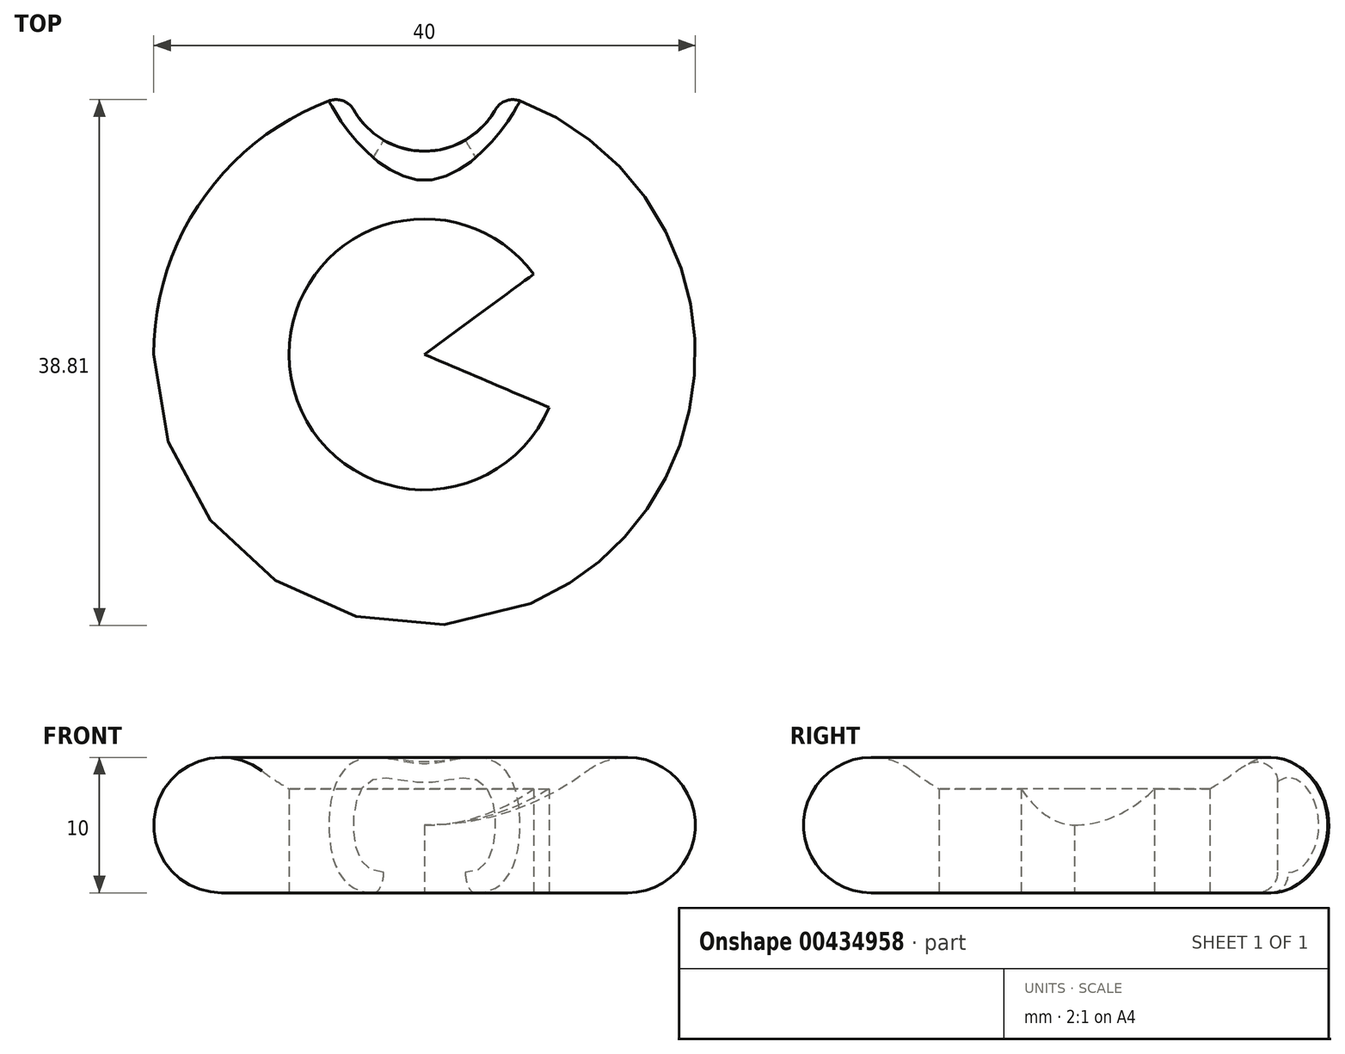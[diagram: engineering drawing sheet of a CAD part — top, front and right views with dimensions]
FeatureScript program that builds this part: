
annotation { "Feature Type Name" : "Feature", "Feature Type Description" : "" }
export const myFeature = defineFeature(function(context is Context, id is Id, definition is map)
    precondition{}
    {
        {
            var Q0;
            Q0=qCreatedBy(makeId("Front.planeOp"),FACE);
            var sketch = newSketch(context, id + "F0", { "sketchPlane" : qUnion([Q0])});
            skArc(sketch, "E0", {"start": v(-12, 9) * mm, "mid": v(-19.74, 6.58) * mm, "end": v(-15, 0) * mm});
            skArc(sketch, "E1", {"start": v(-12, 9) * mm, "mid": v(-6.32, 6.03) * mm, "end": v(0, 5) * mm});
            skLineSegment(sketch, "E2", {"start": v(-15, 0) * mm, "end": v(0, 0) * mm});
            skLineSegment(sketch, "E3", {"start": v(0, 0) * mm, "end": v(0, 5) * mm});
            skPoint(sketch, "E4.orphan", {"position": v(-14.15, 0) * mm});
            skSolve(sketch);
        }
        {
            var Q0;
            Q0=makeQuery(id+"F0.imprint","IMPRINT",FACE,{"disambiguationData":[TD([[makeQuery(id+"F0.imprint","IMPRINT",EDGE,{"derivedFrom":sQuery(id+"F0.wireOp",EDGE,"E0")}),1.0]])]});
            var Q1;
            Q1=sQuery(id+"F0.wireOp",EDGE,"E3");
            revolve(context, id + "F1", {"entities" : qUnion([Q0]), "axis" : qUnion([Q1]), "revolveType" : RevolveType.FULL});
        }
        {
            var Q0;
            Q0=qCreatedBy(makeId("Top.planeOp"),FACE);
            var sketch = newSketch(context, id + "F2", { "sketchPlane" : qUnion([Q0])});
            skCircle(sketch, "E5", {"center": v(0, 21) * mm, "radius": 6 * mm});
            skSolve(sketch);
        }
        {
            var Q0;
            Q0 = qSketchRegion(id + "F2", true);
            extrude(context, id + "F3", {"entities" : qUnion([Q0]), "operationType" : NewBodyOperationType.REMOVE, "depth" : 25 * mm});
        }
        {
            var Q0;
            Q0=makeQuery(id+"F3.boolean.opBoolean","INTERSECT",EDGE,{"derivedFrom":[makeQuery(id+"F1.opRevolve","SWEPT_FACE",FACE,{"disambiguationData":[OSD([sQuery(id+"F0.wireOp",EDGE,"E0")])]}),makeQuery(id+"F3.opExtrude","SWEPT_FACE",FACE,{"disambiguationData":[OSD([sQuery(id+"F2.wireOp",EDGE,"E5")])]})]});
            fillet(context, id + "F4", {"entities" : qUnion([Q0]), "radius" : 1.5 * mm, "tangentPropagation" : true, "allowEdgeOverflow" : false});
        }
        {
            var Q0;
            Q0=qCreatedBy(makeId("Top.planeOp"),FACE);
            var sketch = newSketch(context, id + "F5", { "sketchPlane" : qUnion([Q0])});
            skArc(sketch, "E6", {"start": v(8.06, 5.92) * mm, "mid": v(-9.93, -1.15) * mm, "end": v(9.2, -3.92) * mm});
            skLineSegment(sketch, "E7", {"start": v(8.06, 5.92) * mm, "end": v(0, 0) * mm});
            skLineSegment(sketch, "E8", {"start": v(0, 0) * mm, "end": v(9.2, -3.92) * mm});
            skSolve(sketch);
        }
        {
            var Q0;
            Q0 = qSketchRegion(id + "F5", true);
            extrude(context, id + "F6", {"entities" : qUnion([Q0]), "operationType" : NewBodyOperationType.REMOVE, "depth" : 25 * mm});
        }
    });
